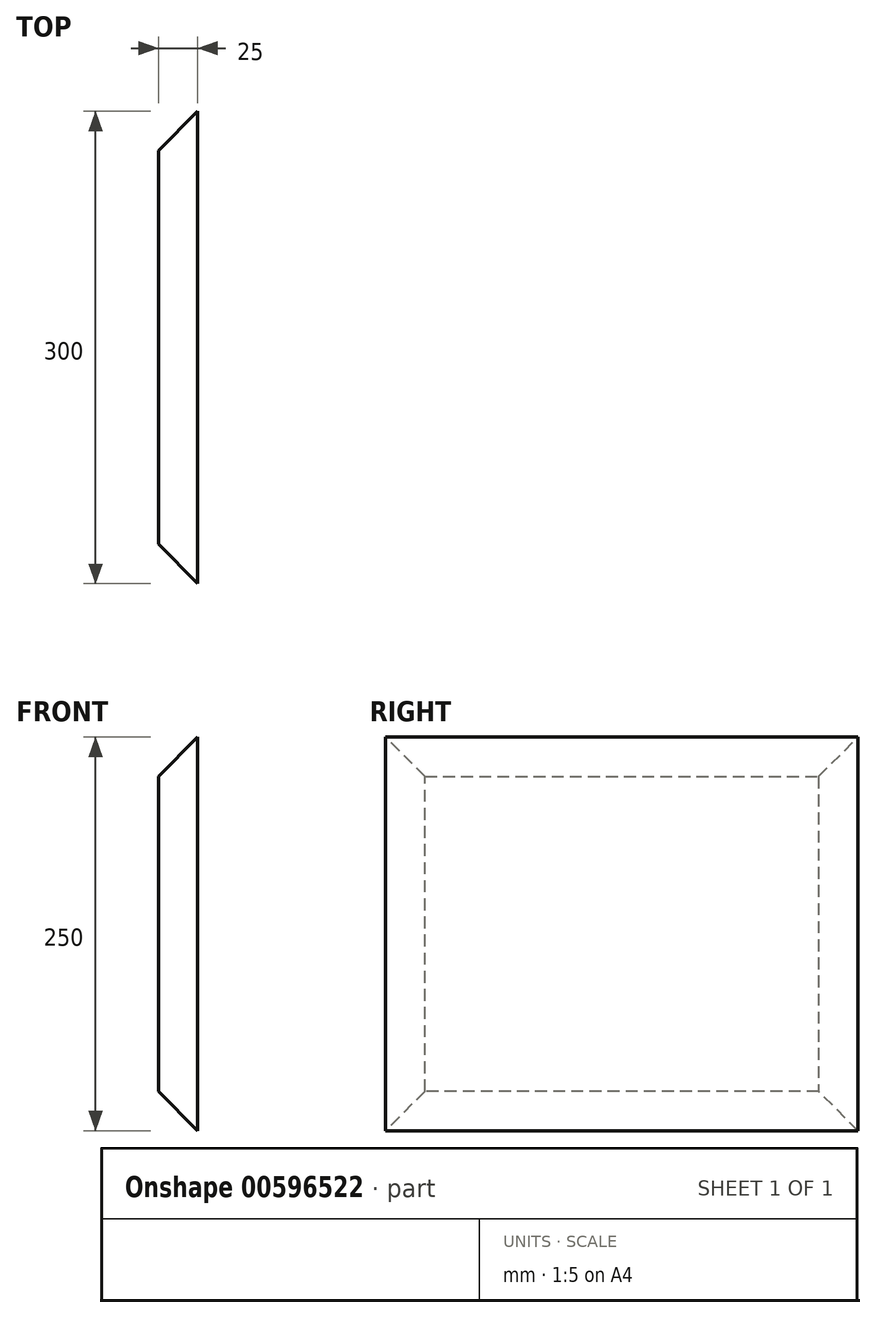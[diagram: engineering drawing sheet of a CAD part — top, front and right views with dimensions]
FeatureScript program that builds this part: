
annotation { "Feature Type Name" : "Feature", "Feature Type Description" : "" }
export const myFeature = defineFeature(function(context is Context, id is Id, definition is map)
    precondition{}
    {
        {
            var Q0;
            Q0=qCreatedBy(makeId("Right.planeOp"),FACE);
            var sketch = newSketch(context, id + "F0", { "sketchPlane" : qUnion([Q0])});
            skLineSegment(sketch, "E0.bottom", {"start": v(150, -125) * mm, "end": v(-150, -125) * mm});
            skLineSegment(sketch, "E0.top", {"start": v(150, 125) * mm, "end": v(-150, 125) * mm});
            skLineSegment(sketch, "E0.left", {"start": v(150, -125) * mm, "end": v(150, 125) * mm});
            skLineSegment(sketch, "E0.right", {"start": v(-150, -125) * mm, "end": v(-150, 125) * mm});
            skPoint(sketch, "E0.middle", {"position": v(0, 0) * mm});
            skSolve(sketch);
        }
        {
            var Q0;
            Q0=makeQuery(id+"F0.imprint","IMPRINT",FACE,{"disambiguationData":[TD([[makeQuery(id+"F0.imprint","IMPRINT",EDGE,{"derivedFrom":sQuery(id+"F0.wireOp",EDGE,"E0.bottom")}),-1.0]])]});
            extrude(context, id + "F1", {"entities" : qUnion([Q0]), "oppositeDirection" : true, "depth" : 25 * mm, "offsetDistance" : 25 * mm});
        }
        {
            var Q0;
            Q0=makeQuery(id+"F1.opExtrude","CAP_EDGE",EDGE,{"disambiguationData":[OSD([sQuery(id+"F0.wireOp",EDGE,"E0.top")])],"isStart":false});
            var Q1;
            Q1=makeQuery(id+"F1.opExtrude","CAP_EDGE",EDGE,{"disambiguationData":[OSD([sQuery(id+"F0.wireOp",EDGE,"E0.right")])],"isStart":false});
            var Q2;
            Q2=makeQuery(id+"F1.opExtrude","CAP_EDGE",EDGE,{"disambiguationData":[OSD([sQuery(id+"F0.wireOp",EDGE,"E0.bottom")])],"isStart":false});
            var Q3;
            Q3=makeQuery(id+"F1.opExtrude","CAP_EDGE",EDGE,{"disambiguationData":[OSD([sQuery(id+"F0.wireOp",EDGE,"E0.left")])],"isStart":false});
            chamfer(context, id + "F2", {"entities" : qUnion([Q0, Q1, Q2, Q3]), "width" : 25 * mm, "tangentPropagation" : true});
        }
    });
